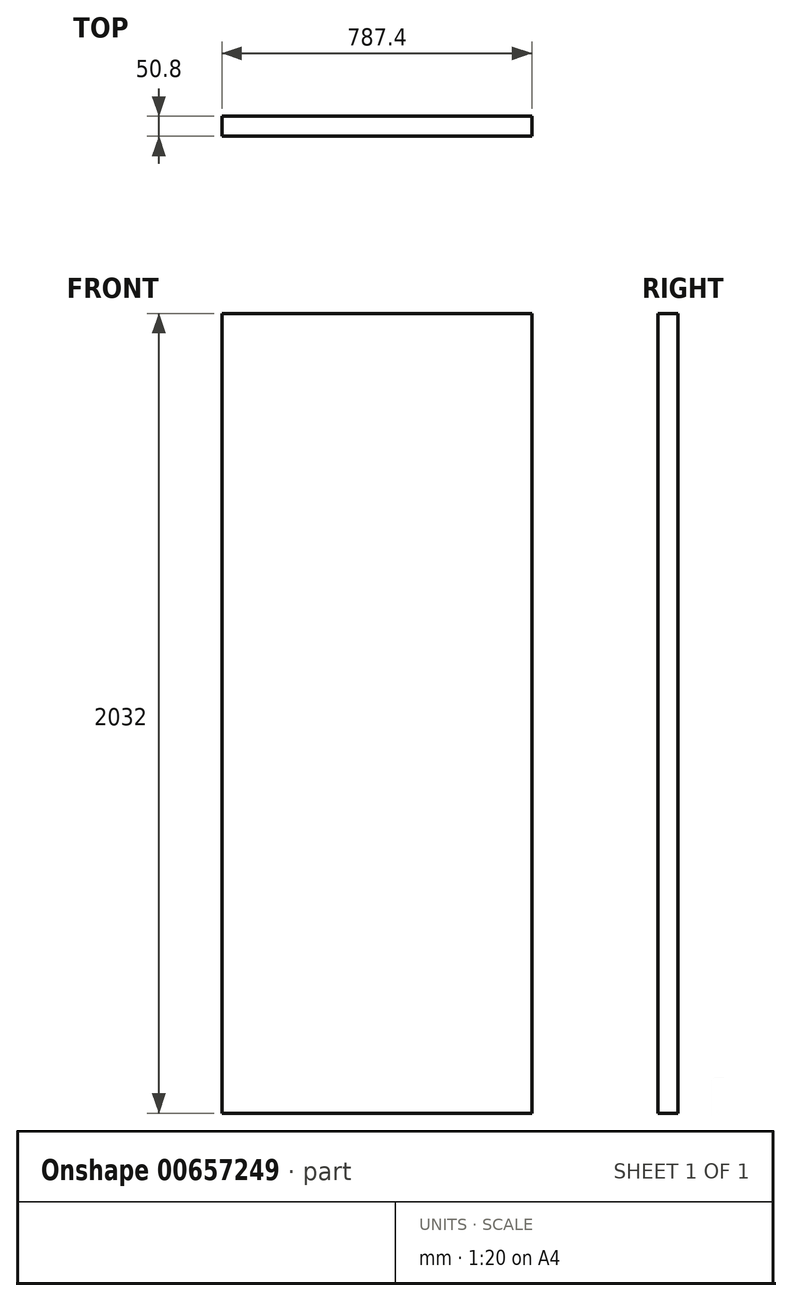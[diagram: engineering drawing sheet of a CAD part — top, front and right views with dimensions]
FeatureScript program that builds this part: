
annotation { "Feature Type Name" : "Feature", "Feature Type Description" : "" }
export const myFeature = defineFeature(function(context is Context, id is Id, definition is map)
    precondition{}
    {
        {
            var Q0;
            Q0=qCreatedBy(makeId("Front.planeOp"),FACE);
            var sketch = newSketch(context, id + "F0", { "sketchPlane" : qUnion([Q0])});
            skLineSegment(sketch, "E0.bottom", {"start": v(-393.7, 1016) * mm, "end": v(393.7, 1016) * mm});
            skLineSegment(sketch, "E0.top", {"start": v(-393.7, -1016) * mm, "end": v(393.7, -1016) * mm});
            skLineSegment(sketch, "E0.left", {"start": v(-393.7, 1016) * mm, "end": v(-393.7, -1016) * mm});
            skLineSegment(sketch, "E0.right", {"start": v(393.7, 1016) * mm, "end": v(393.7, -1016) * mm});
            skSolve(sketch);
        }
        {
            var Q0;
            Q0=qSketchRegion(id+"F0",true);
            extrude(context, id + "F1", {"entities" : qUnion([Q0]), "depth" : 50.8 * mm, "offsetDistance" : 25.4 * mm});
        }
    });
